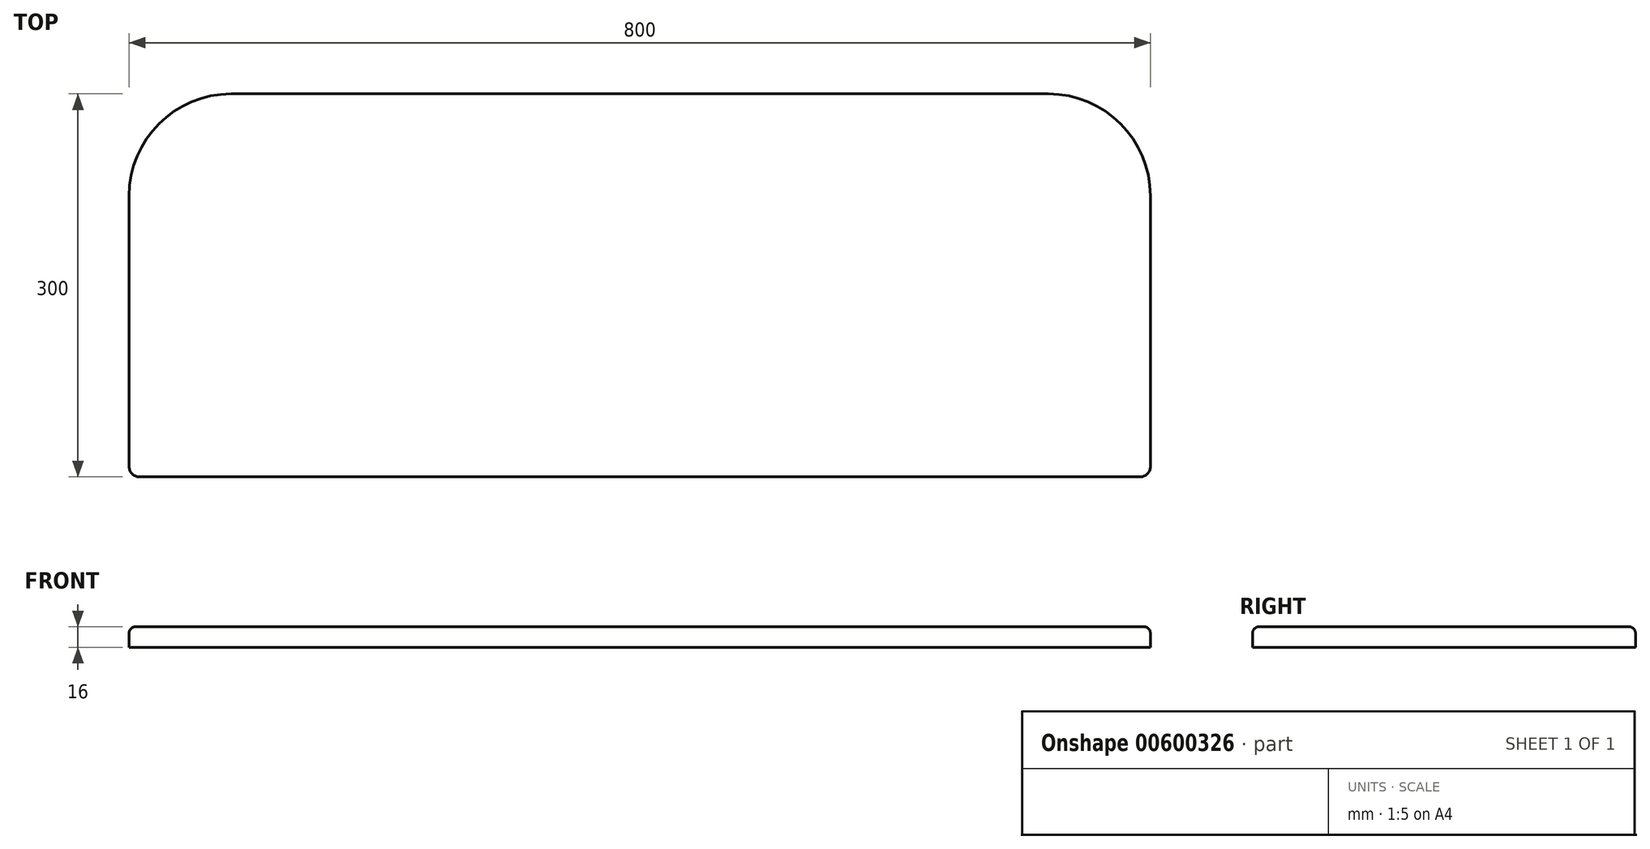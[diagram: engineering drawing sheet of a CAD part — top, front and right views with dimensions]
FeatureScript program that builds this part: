
annotation { "Feature Type Name" : "Feature", "Feature Type Description" : "" }
export const myFeature = defineFeature(function(context is Context, id is Id, definition is map)
    precondition{}
    {
        {
            var Q0;
            Q0=qCreatedBy(makeId("Top.planeOp"),FACE);
            var sketch = newSketch(context, id + "F0", { "sketchPlane" : qUnion([Q0])});
            skLineSegment(sketch, "E0.bottom", {"start": v(800, 0) * mm, "end": v(0, 0) * mm});
            skLineSegment(sketch, "E0.top", {"start": v(800, 300) * mm, "end": v(0, 300) * mm});
            skLineSegment(sketch, "E0.left", {"start": v(800, 0) * mm, "end": v(800, 300) * mm});
            skLineSegment(sketch, "E0.right", {"start": v(0, 0) * mm, "end": v(0, 300) * mm});
            skSolve(sketch);
        }
        {
            var Q0;
            Q0=makeQuery(id+"F0.imprint","IMPRINT",FACE,{"disambiguationData":[TD([[makeQuery(id+"F0.imprint","IMPRINT",EDGE,{"derivedFrom":sQuery(id+"F0.wireOp",EDGE,"E0.bottom")}),-1.0]])]});
            extrude(context, id + "F1", {"entities" : qUnion([Q0]), "oppositeDirection" : true, "depth" : 16 * mm, "offsetDistance" : 25 * mm});
        }
        {
            var Q0;
            Q0=makeQuery(id+"F1.opExtrude","SWEPT_EDGE",EDGE,{"disambiguationData":[OSD([sQuery(id+"F0.wireOp",EDGE,"E0.top"),sQuery(id+"F0.wireOp",EDGE,"E0.right")])]});
            fillet(context, id + "F2", {"entities" : qUnion([Q0]), "radius" : 80 * mm, "tangentPropagation" : true, "allowEdgeOverflow" : false});
        }
        {
            var Q0;
            Q0=makeQuery(id+"F1.opExtrude","SWEPT_EDGE",EDGE,{"disambiguationData":[OSD([sQuery(id+"F0.wireOp",EDGE,"E0.top"),sQuery(id+"F0.wireOp",EDGE,"E0.left")])]});
            fillet(context, id + "F3", {"entities" : qUnion([Q0]), "radius" : 80 * mm, "tangentPropagation" : true, "allowEdgeOverflow" : false});
        }
        {
            var Q0;
            Q0=makeQuery(id+"F1.opExtrude","SWEPT_EDGE",EDGE,{"disambiguationData":[OSD([sQuery(id+"F0.wireOp",EDGE,"E0.bottom"),sQuery(id+"F0.wireOp",EDGE,"E0.left")])]});
            var Q1;
            Q1=makeQuery(id+"F1.opExtrude","SWEPT_EDGE",EDGE,{"disambiguationData":[OSD([sQuery(id+"F0.wireOp",EDGE,"E0.bottom"),sQuery(id+"F0.wireOp",EDGE,"E0.right")])]});
            fillet(context, id + "F4", {"entities" : qUnion([Q0, Q1]), "radius" : 8 * mm, "tangentPropagation" : true, "allowEdgeOverflow" : false});
        }
        {
            var Q0;
            Q0=makeQuery(id+"F1.opExtrude","CAP_EDGE",EDGE,{"disambiguationData":[OSD([sQuery(id+"F0.wireOp",EDGE,"E0.top")])],"isStart":true});
            fillet(context, id + "F5", {"entities" : qUnion([Q0]), "radius" : 5 * mm, "tangentPropagation" : true, "allowEdgeOverflow" : false});
        }
    });
